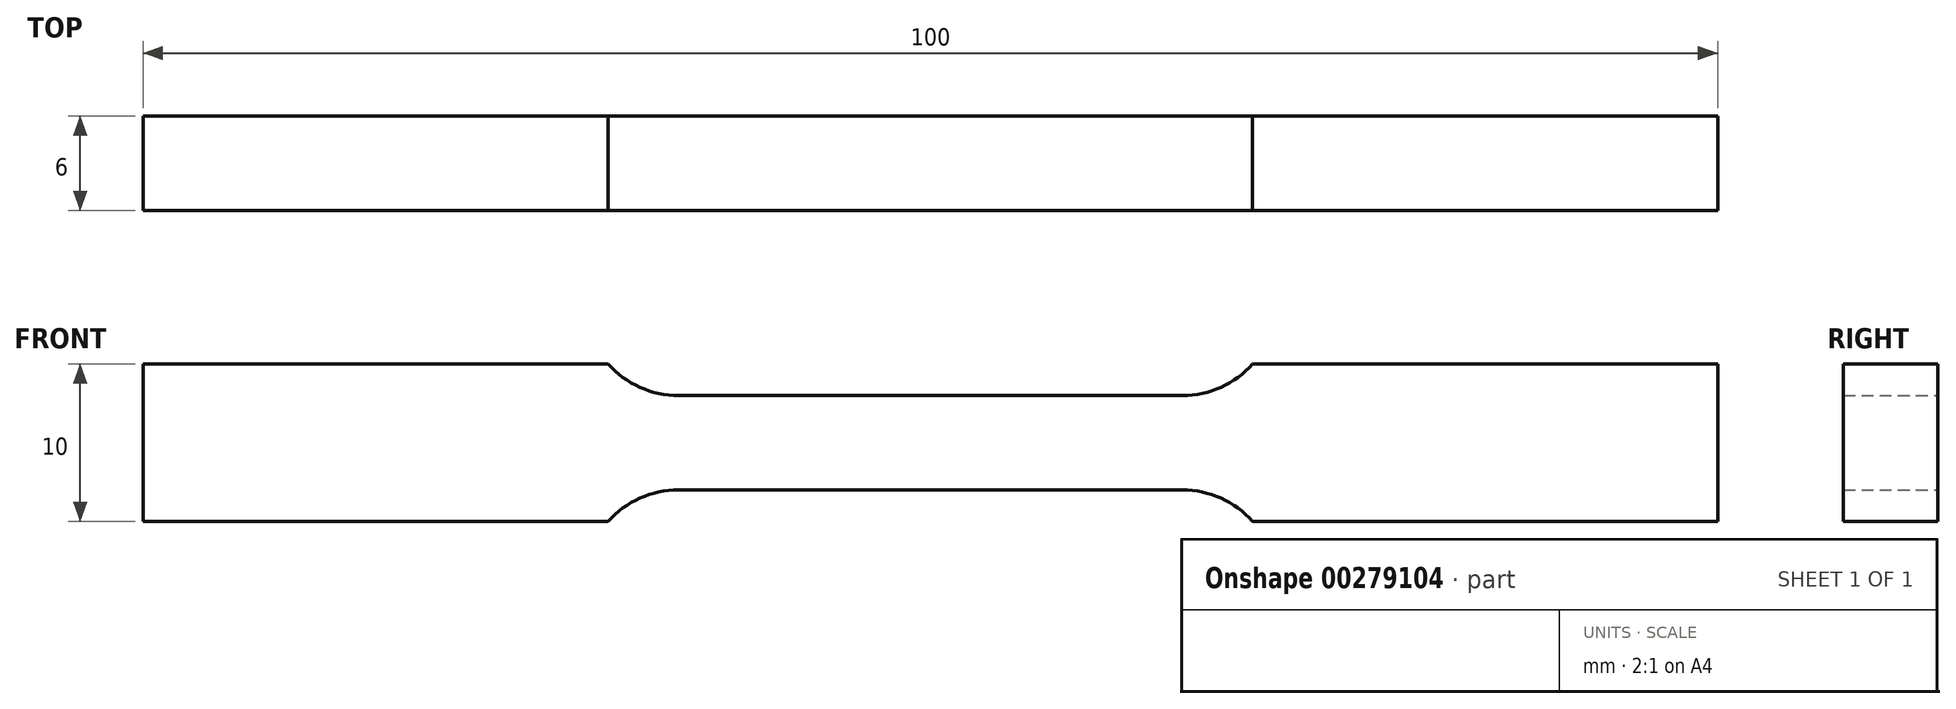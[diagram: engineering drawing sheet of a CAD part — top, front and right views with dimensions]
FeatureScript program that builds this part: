
annotation { "Feature Type Name" : "Feature", "Feature Type Description" : "" }
export const myFeature = defineFeature(function(context is Context, id is Id, definition is map)
    precondition{}
    {
        {
            var Q0;
            Q0=qCreatedBy(makeId("Front.planeOp"),FACE);
            var sketch = newSketch(context, id + "F0", { "sketchPlane" : qUnion([Q0])});
            skLineSegment(sketch, "E0", {"start": v(0, 3) * mm, "end": v(16, 3) * mm});
            skArc(sketch, "E1", {"start": v(16, 3) * mm, "mid": v(18.45, 3.52) * mm, "end": v(20.47, 5) * mm});
            skLineSegment(sketch, "E2", {"start": v(20.47, 5) * mm, "end": v(50, 5) * mm});
            skLineSegment(sketch, "E3.MirrorCS", {"start": v(20.47, -5) * mm, "end": v(50, -5) * mm});
            skLineSegment(sketch, "E4.MirrorCS", {"start": v(0, -3) * mm, "end": v(16, -3) * mm});
            skArc(sketch, "E5.MirrorCS", {"start": v(16, -3) * mm, "mid": v(18.45, -3.52) * mm, "end": v(20.47, -5) * mm});
            skLineSegment(sketch, "E6.MirrorCS", {"start": v(0, 3) * mm, "end": v(-16, 3) * mm});
            skArc(sketch, "E7.MirrorCS", {"start": v(-16, 3) * mm, "mid": v(-18.45, 3.52) * mm, "end": v(-20.47, 5) * mm});
            skLineSegment(sketch, "E8.MirrorCS", {"start": v(-20.47, 5) * mm, "end": v(-50, 5) * mm});
            skLineSegment(sketch, "E9.MirrorCS", {"start": v(-20.47, -5) * mm, "end": v(-50, -5) * mm});
            skArc(sketch, "E10.MirrorCS", {"start": v(-16, -3) * mm, "mid": v(-18.45, -3.52) * mm, "end": v(-20.47, -5) * mm});
            skLineSegment(sketch, "E11.MirrorCS", {"start": v(0, -3) * mm, "end": v(-16, -3) * mm});
            skLineSegment(sketch, "E12", {"start": v(-50, 5) * mm, "end": v(-50, -5) * mm});
            skLineSegment(sketch, "E13", {"start": v(50, 5) * mm, "end": v(50, -5) * mm});
            skSolve(sketch);
        }
        {
            var Q0;
            Q0=makeQuery(id+"F0.imprint","IMPRINT",FACE,{"disambiguationData":[TD([[makeQuery(id+"F0.imprint","IMPRINT",EDGE,{"derivedFrom":sQuery(id+"F0.wireOp",EDGE,"E1")}),-1.0]])]});
            extrude(context, id + "F1", {"entities" : qUnion([Q0]), "endBound" : BoundingType.SYMMETRIC, "depth" : 6 * mm});
        }
    });
